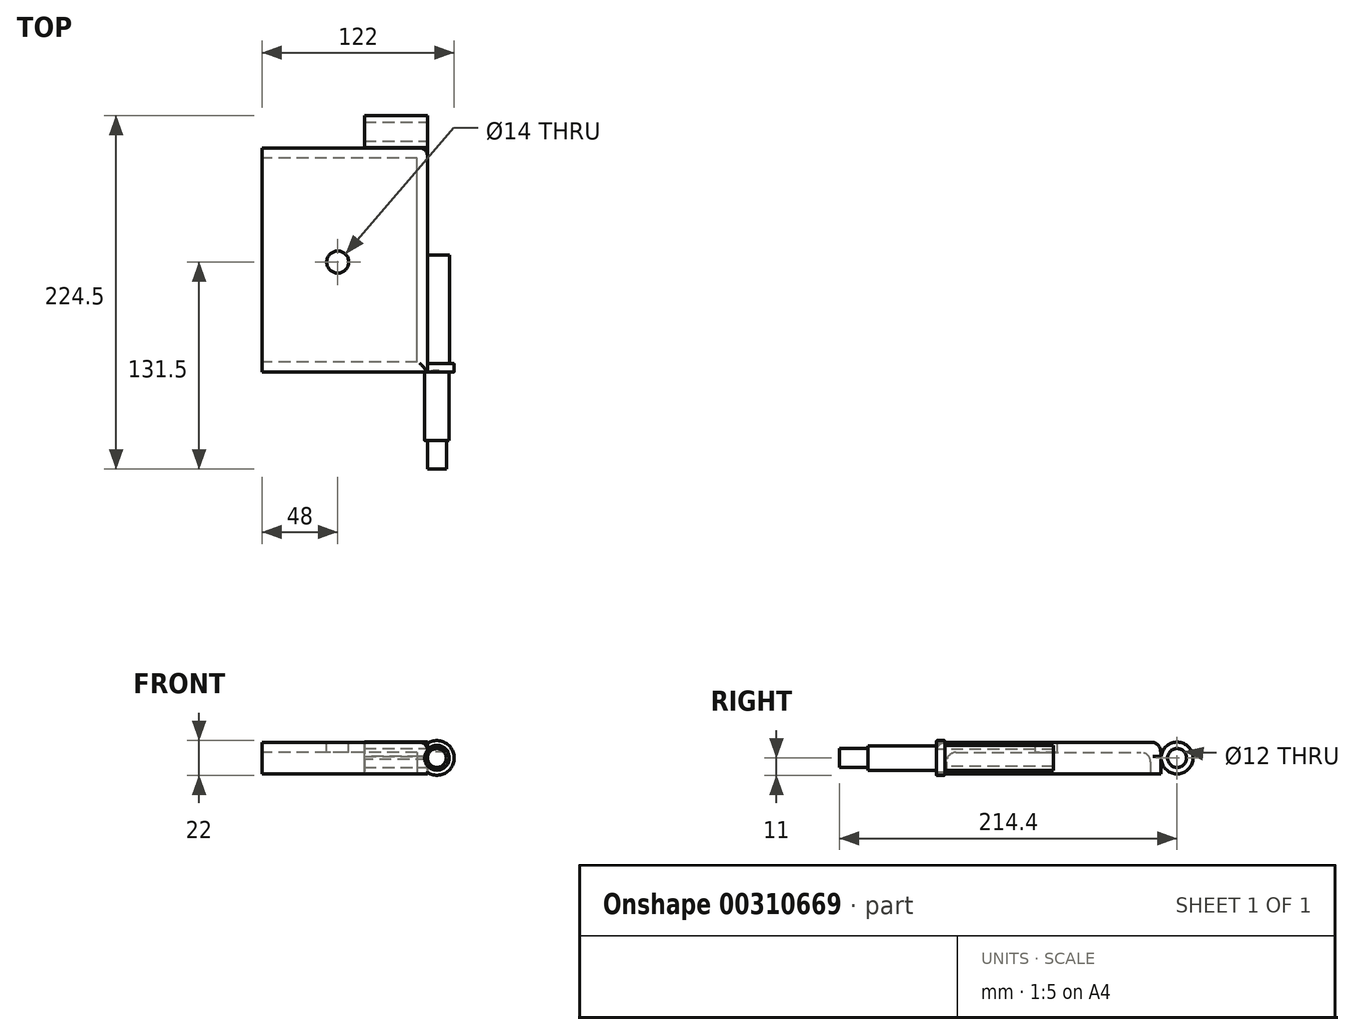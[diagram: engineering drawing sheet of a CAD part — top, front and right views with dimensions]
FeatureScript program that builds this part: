
annotation { "Feature Type Name" : "Feature", "Feature Type Description" : "" }
export const myFeature = defineFeature(function(context is Context, id is Id, definition is map)
    precondition{}
    {
        {
            var Q0;
            Q0=qCreatedBy(makeId("Front.planeOp"),FACE);
            var sketch = newSketch(context, id + "F0", { "sketchPlane" : qUnion([Q0])});
            skLineSegment(sketch, "E0.bottom", {"start": v(52.5, 10) * mm, "end": v(-52.5, 10) * mm});
            skLineSegment(sketch, "E0.top", {"start": v(52.5, -10) * mm, "end": v(-52.5, -10) * mm});
            skLineSegment(sketch, "E0.left", {"start": v(52.5, 10) * mm, "end": v(52.5, -10) * mm});
            skLineSegment(sketch, "E0.right", {"start": v(-52.5, 10) * mm, "end": v(-52.5, -10) * mm});
            skPoint(sketch, "E0.middle", {"position": v(0, 0) * mm});
            skSolve(sketch);
        }
        {
            var Q0;
            Q0=qSketchRegion(id+"F0",true);
            extrude(context, id + "F1", {"entities" : qUnion([Q0]), "depth" : 142.5 * mm});
        }
        {
            var Q0;
            Q0=makeQuery(id+"F1.opExtrude","CAP_FACE",FACE,{"disambiguationData":[OSD([sQuery(id+"F0.wireOp",EDGE,"E0.bottom"),sQuery(id+"F0.wireOp",EDGE,"E0.top"),sQuery(id+"F0.wireOp",EDGE,"E0.left"),sQuery(id+"F0.wireOp",EDGE,"E0.right")])],"isStart":false});
            var sketch = newSketch(context, id + "F2", { "sketchPlane" : qUnion([Q0])});
            skPoint(sketch, "E1", {"position": v(58.5, 0) * mm});
            skCircle(sketch, "E2", {"center": v(58.5, 0) * mm, "radius": 8 * mm});
            skSolve(sketch);
        }
        {
            var Q0;
            Q0=qSketchRegion(id+"F2",true);
            extrude(context, id + "F3", {"entities" : qUnion([Q0]), "operationType" : NewBodyOperationType.ADD, "oppositeDirection" : true, "depth" : 74.5 * mm});
        }
        {
            var Q0;
            Q0=makeQuery(id+"F3.boolean.opBoolean","MERGE",FACE,{"derivedFrom":[makeQuery(id+"F1.opExtrude","CAP_FACE",FACE,{"disambiguationData":[OSD([sQuery(id+"F0.wireOp",EDGE,"E0.bottom"),sQuery(id+"F0.wireOp",EDGE,"E0.top"),sQuery(id+"F0.wireOp",EDGE,"E0.left"),sQuery(id+"F0.wireOp",EDGE,"E0.right")])],"isStart":false}),makeQuery(id+"F3.opExtrude","CAP_FACE",FACE,{"disambiguationData":[OSD([sQuery(id+"F2.wireOp",EDGE,"E2")])],"isStart":true})]});
            var sketch = newSketch(context, id + "F4", { "sketchPlane" : qUnion([Q0])});
            skArc(sketch, "E3.0", {"start": v(52.5, -5.3) * mm, "mid": v(66.5, 0) * mm, "end": v(52.5, 5.3) * mm});
            skCircle(sketch, "E4", {"center": v(58.5, 0) * mm, "radius": 7.75 * mm});
            skCircle(sketch, "E5", {"center": v(58.5, 0) * mm, "radius": 11 * mm});
            skSolve(sketch);
        }
        {
            var Q0;
            Q0=makeQuery(id+"F4.imprint","IMPRINT",FACE,{"disambiguationData":[TD([[makeQuery(id+"F4.imprint","IMPRINT",EDGE,{"derivedFrom":sQuery(id+"F4.wireOp",EDGE,"E4")}),1.0]])]});
            extrude(context, id + "F5", {"entities" : qUnion([Q0]), "operationType" : NewBodyOperationType.ADD, "depth" : 43.5 * mm});
        }
        {
            var Q0;
            Q0=makeQuery(id+"F5.opExtrude","CAP_FACE",FACE,{"disambiguationData":[OSD([sQuery(id+"F4.wireOp",EDGE,"E4")])],"isStart":false});
            var sketch = newSketch(context, id + "F6", { "sketchPlane" : qUnion([Q0])});
            skCircle(sketch, "E6.0", {"center": v(58.5, 0) * mm, "radius": 7.75 * mm});
            skCircle(sketch, "E7", {"center": v(58.5, 0) * mm, "radius": 6 * mm});
            skSolve(sketch);
        }
        {
            var Q0;
            Q0=makeQuery(id+"F6.imprint","IMPRINT",FACE,{"disambiguationData":[TD([[makeQuery(id+"F6.imprint","IMPRINT",EDGE,{"derivedFrom":sQuery(id+"F6.wireOp",EDGE,"E7")}),1.0]])]});
            extrude(context, id + "F7", {"entities" : qUnion([Q0]), "operationType" : NewBodyOperationType.ADD, "depth" : 18 * mm});
        }
        {
            var Q0;
            Q0=makeQuery(id+"F1.opExtrude","SWEPT_FACE",FACE,{"disambiguationData":[OSD([sQuery(id+"F0.wireOp",EDGE,"E0.left")])]});
            var sketch = newSketch(context, id + "F8", { "sketchPlane" : qUnion([Q0])});
            skPoint(sketch, "E8", {"position": v(10.4, 0) * mm});
            skCircle(sketch, "E9", {"center": v(10.4, 0) * mm, "radius": 10.1 * mm});
            skCircle(sketch, "E10", {"center": v(10.4, 0) * mm, "radius": 6 * mm});
            skPoint(sketch, "E11", {"position": v(0, 0) * mm});
            skLineSegment(sketch, "E12.bottom", {"start": v(1, 1) * mm, "end": v(-1, 1) * mm});
            skLineSegment(sketch, "E12.top", {"start": v(1, -1) * mm, "end": v(-1, -1) * mm});
            skLineSegment(sketch, "E12.left", {"start": v(1, 1) * mm, "end": v(1, -1) * mm});
            skLineSegment(sketch, "E12.right", {"start": v(-1, 1) * mm, "end": v(-1, -1) * mm});
            skSolve(sketch);
        }
        {
            var Q0;
            {var subQ5=sQuery(id+"F8.wireOp",EDGE,"E12.left");Q0=makeQuery(id+"F8.imprint","IMPRINT",FACE,{"disambiguationData":[TD([[makeQuery(id+"F8.imprint","IMPRINT",EDGE,{"derivedFrom":subQ5}),-1.0]])]});}
            var Q1;
            {var subQ0=sQuery(id+"F8.wireOp",EDGE,"E12.right");Q1=makeQuery(id+"F8.imprint","IMPRINT",FACE,{"disambiguationData":[TD([[makeQuery(id+"F8.imprint","IMPRINT",EDGE,{"derivedFrom":subQ0}),1.0]])]});}
            var Q2;
            {var subQ0=sQuery(id+"F8.wireOp",EDGE,"E12.bottom");var subQ1=sQuery(id+"F8.wireOp",EDGE,"E9");var subQ2=makeQuery(id+"F8.imprint","INTERSECT",VERTEX,{"derivedFrom":[subQ1,subQ0]});Q2=makeQuery(id+"F8.imprint","IMPRINT",FACE,{"disambiguationData":[TD([[makeQuery(id+"F8.imprint","IMPRINT",EDGE,{"disambiguationData":[TD([[subQ2,-1.0]])],"derivedFrom":subQ1}),-1.0]])]});}
            var Q3;
            Q3=makeQuery(id+"F8.imprint","IMPRINT",FACE,{"disambiguationData":[TD([[makeQuery(id+"F8.imprint","IMPRINT",EDGE,{"derivedFrom":sQuery(id+"F8.wireOp",EDGE,"E10")}),-1.0]])]});
            extrude(context, id + "F9", {"entities" : qUnion([Q0, Q1, Q2, Q3]), "operationType" : NewBodyOperationType.ADD, "oppositeDirection" : true, "depth" : 40 * mm});
        }
        {
            var Q0;
            Q0=makeQuery(id+"F1.opExtrude","SWEPT_FACE",FACE,{"disambiguationData":[OSD([sQuery(id+"F0.wireOp",EDGE,"E0.right")])]});
            var sketch = newSketch(context, id + "F10", { "sketchPlane" : qUnion([Q0])});
            skLineSegment(sketch, "E13.0", {"start": v(136.5, 10) * mm, "end": v(6, 10) * mm});
            skLineSegment(sketch, "E14.0", {"start": v(142.5, 4) * mm, "end": v(142.5, -10) * mm});
            skLineSegment(sketch, "E15.0", {"start": v(0, 4) * mm, "end": v(0, -10) * mm});
            skLineSegment(sketch, "E16.0", {"start": v(142.5, -10) * mm, "end": v(0, -10) * mm});
            skLineSegment(sketch, "E17.0", {"start": v(6.5, -2.5) * mm, "end": v(6.5, -10) * mm});
            skLineSegment(sketch, "E17.1", {"start": v(130, 3.5) * mm, "end": v(12.5, 3.5) * mm});
            skLineSegment(sketch, "E17.2", {"start": v(136, -2.5) * mm, "end": v(136, -10) * mm});
            skPoint(sketch, "E18.visualSharp", {"position": v(0, 10) * mm});
            skArc(sketch, "E18.filletArc", {"start": v(6, 10) * mm, "mid": v(1.76, 8.24) * mm, "end": v(0, 4) * mm});
            skPoint(sketch, "E19.visualSharp", {"position": v(6.5, 3.5) * mm});
            skArc(sketch, "E19.filletArc", {"start": v(12.5, 3.5) * mm, "mid": v(8.26, 1.74) * mm, "end": v(6.5, -2.5) * mm});
            skPoint(sketch, "E20.visualSharp", {"position": v(142.5, 10) * mm});
            skArc(sketch, "E20.filletArc", {"start": v(142.5, 4) * mm, "mid": v(140.74, 8.24) * mm, "end": v(136.5, 10) * mm});
            skPoint(sketch, "E21.visualSharp", {"position": v(136, 3.5) * mm});
            skArc(sketch, "E21.filletArc", {"start": v(136, -2.5) * mm, "mid": v(134.24, 1.74) * mm, "end": v(130, 3.5) * mm});
            skLineSegment(sketch, "E22", {"start": v(136.5, 10) * mm, "end": v(142.5, 10) * mm});
            skLineSegment(sketch, "E23", {"start": v(6, 10) * mm, "end": v(0, 10) * mm});
            skLineSegment(sketch, "E24", {"start": v(0, 4) * mm, "end": v(0, 10) * mm});
            skLineSegment(sketch, "E25", {"start": v(142.5, 4) * mm, "end": v(142.5, 10) * mm});
            skSolve(sketch);
        }
        {
            var Q0;
            {var subQ1=sQuery(id+"F10.wireOp",EDGE,"E17.0");Q0=makeQuery(id+"F10.imprint","IMPRINT",FACE,{"disambiguationData":[TD([[makeQuery(id+"F10.imprint","IMPRINT",EDGE,{"derivedFrom":subQ1}),1.0]])]});}
            var Q1;
            Q1=makeQuery(id+"F10.imprint","IMPRINT",FACE,{"disambiguationData":[TD([[makeQuery(id+"F10.imprint","IMPRINT",EDGE,{"derivedFrom":sQuery(id+"F10.wireOp",EDGE,"E20.filletArc")}),-1.0]])]});
            var Q2;
            Q2=makeQuery(id+"F10.imprint","IMPRINT",FACE,{"disambiguationData":[TD([[makeQuery(id+"F10.imprint","IMPRINT",EDGE,{"derivedFrom":sQuery(id+"F10.wireOp",EDGE,"E18.filletArc")}),-1.0]])]});
            extrude(context, id + "F11", {"entities" : qUnion([Q0, Q1, Q2]), "operationType" : NewBodyOperationType.REMOVE, "oppositeDirection" : true, "depth" : 98.5 * mm});
        }
        {
            var Q0;
            Q0=makeQuery(id+"F11.boolean.opBoolean","COPY",FACE,{"derivedFrom":makeQuery(id+"F11.opExtrude","CAP_FACE",FACE,{"disambiguationData":[OSD([sQuery(id+"F10.wireOp",EDGE,"E20.filletArc"),sQuery(id+"F10.wireOp",EDGE,"E22"),sQuery(id+"F10.wireOp",EDGE,"E25")])],"isStart":false})});
            var sketch = newSketch(context, id + "F12", { "sketchPlane" : qUnion([Q0])});
            skArc(sketch, "E26.0", {"start": v(142.5, 4) * mm, "mid": v(140.74, 8.24) * mm, "end": v(136.5, 10) * mm});
            skLineSegment(sketch, "E27.0", {"start": v(142.5, 10) * mm, "end": v(136.5, 10) * mm});
            skLineSegment(sketch, "E28.0", {"start": v(142.5, 10) * mm, "end": v(142.5, 4) * mm});
            skArc(sketch, "E29.0.0", {"start": v(0, 4) * mm, "mid": v(1.76, 8.24) * mm, "end": v(6, 10) * mm});
            skLineSegment(sketch, "E29.0.1", {"start": v(6, 10) * mm, "end": v(0, 10) * mm});
            skLineSegment(sketch, "E29.0.2", {"start": v(0, 10) * mm, "end": v(0, 4) * mm});
            skSolve(sketch);
        }
        {
            var Q0;
            Q0=qSketchRegion(id+"F12",true);
            extrude(context, id + "F13", {"entities" : qUnion([Q0]), "operationType" : NewBodyOperationType.REMOVE, "oppositeDirection" : true, "depth" : 25 * mm});
        }
        {
            var Q0;
            Q0=makeQuery(id+"F1.opExtrude","SWEPT_FACE",FACE,{"disambiguationData":[OSD([sQuery(id+"F0.wireOp",EDGE,"E0.bottom")])]});
            var sketch = newSketch(context, id + "F14", { "sketchPlane" : qUnion([Q0])});
            skPoint(sketch, "E30", {"position": v(-4.5, -72.5) * mm});
            skCircle(sketch, "E31", {"center": v(-4.5, -72.5) * mm, "radius": 7 * mm});
            skSolve(sketch);
        }
        {
            var Q0;
            Q0=qSketchRegion(id+"F14",true);
            extrude(context, id + "F15", {"entities" : qUnion([Q0]), "operationType" : NewBodyOperationType.REMOVE, "oppositeDirection" : true, "depth" : 7 * mm});
        }
        {
            var Q0;
            Q0=makeQuery(id+"F13.boolean.opBoolean","INTERSECT",EDGE,{"derivedFrom":[makeQuery(id+"F9.boolean.opBoolean","MERGE",FACE,{"derivedFrom":[makeQuery(id+"F1.opExtrude","SWEPT_FACE",FACE,{"disambiguationData":[OSD([sQuery(id+"F0.wireOp",EDGE,"E0.left")])]}),makeQuery(id+"F9.opExtrude","CAP_FACE",FACE,{"disambiguationData":[OSD([sQuery(id+"F8.wireOp",EDGE,"E9"),sQuery(id+"F8.wireOp",EDGE,"E10"),sQuery(id+"F8.wireOp",EDGE,"E12.bottom"),sQuery(id+"F8.wireOp",EDGE,"E12.top"),sQuery(id+"F8.wireOp",EDGE,"E12.right")])],"isStart":true})]}),makeQuery(id+"F13.opExtrude","SWEPT_FACE",FACE,{"disambiguationData":[OSD([sQuery(id+"F12.wireOp",EDGE,"E26.0")])]})]});
            fillet(context, id + "F16", {"entities" : qUnion([Q0]), "radius" : 5 * mm, "tangentPropagation" : true, "allowEdgeOverflow" : false});
        }
        {
            var Q0;
            {var subQ0=sQuery(id+"F4.wireOp",EDGE,"E3.0");Q0=makeQuery(id+"F4.imprint","IMPRINT",FACE,{"disambiguationData":[TD([[makeQuery(id+"F4.imprint","IMPRINT",EDGE,{"derivedFrom":subQ0}),-1.0]])]});}
            extrude(context, id + "F17", {"entities" : qUnion([Q0]), "operationType" : NewBodyOperationType.ADD, "oppositeDirection" : true, "depth" : 5.5 * mm});
        }
        {
            var Q0;
            Q0=makeQuery(id+"F17.opExtrude","CAP_EDGE",EDGE,{"disambiguationData":[OSD([sQuery(id+"F4.wireOp",EDGE,"E5")])],"isStart":true});
            var Q1;
            Q1=makeQuery(id+"F17.opExtrude","CAP_EDGE",EDGE,{"disambiguationData":[OSD([sQuery(id+"F4.wireOp",EDGE,"E5")])],"isStart":false});
            fillet(context, id + "F18", {"entities" : qUnion([Q0, Q1]), "radius" : .5 * mm, "tangentPropagation" : true, "allowEdgeOverflow" : false});
        }
    });
